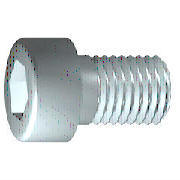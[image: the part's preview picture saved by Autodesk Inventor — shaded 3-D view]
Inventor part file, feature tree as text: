
AUTODESK INVENTOR PART (.ipt)
format: ipt  version: 2019 (Build 230136000, 136)  size: 195,072 bytes
history: native  units: mm (DEFAULTED — no unit token found)
features: sketch x2, extrude x1, plane x1, fillet x1
ambient origin geometry x7: Origin, YZ Plane, XY Plane, X Axis, Y Axis, Z Axis, Center Point
bodies: Solid1 (feature_tree), Body (feature_tree)
feature tree (5):
  extrude  "Slot"  Depth=5.0mm
  plane  "Work Plane1"
  fillet  "Fillet2"  Radius=5.0mm
  sketch  "Sketch1"  dims[d1=18.0mm d2=0.49086mm d3=5.0mm]
  sketch  "Sketch2"  dims[d4=2.5mm d5=60.0deg d6=5.0mm d7=5.0mm d8=4.618802mm d9=8.5mm d10=90.0deg d11=10.0mm d12=0.0mm d13=18.0mm d14=0.0mm d15=0.49076mm d16=0.49076mm d17=0.5mm d19=0.0mm d26=20.0mm d27=45.0deg d28=0.0mm d29=0.0mm d30=0.1mm]
